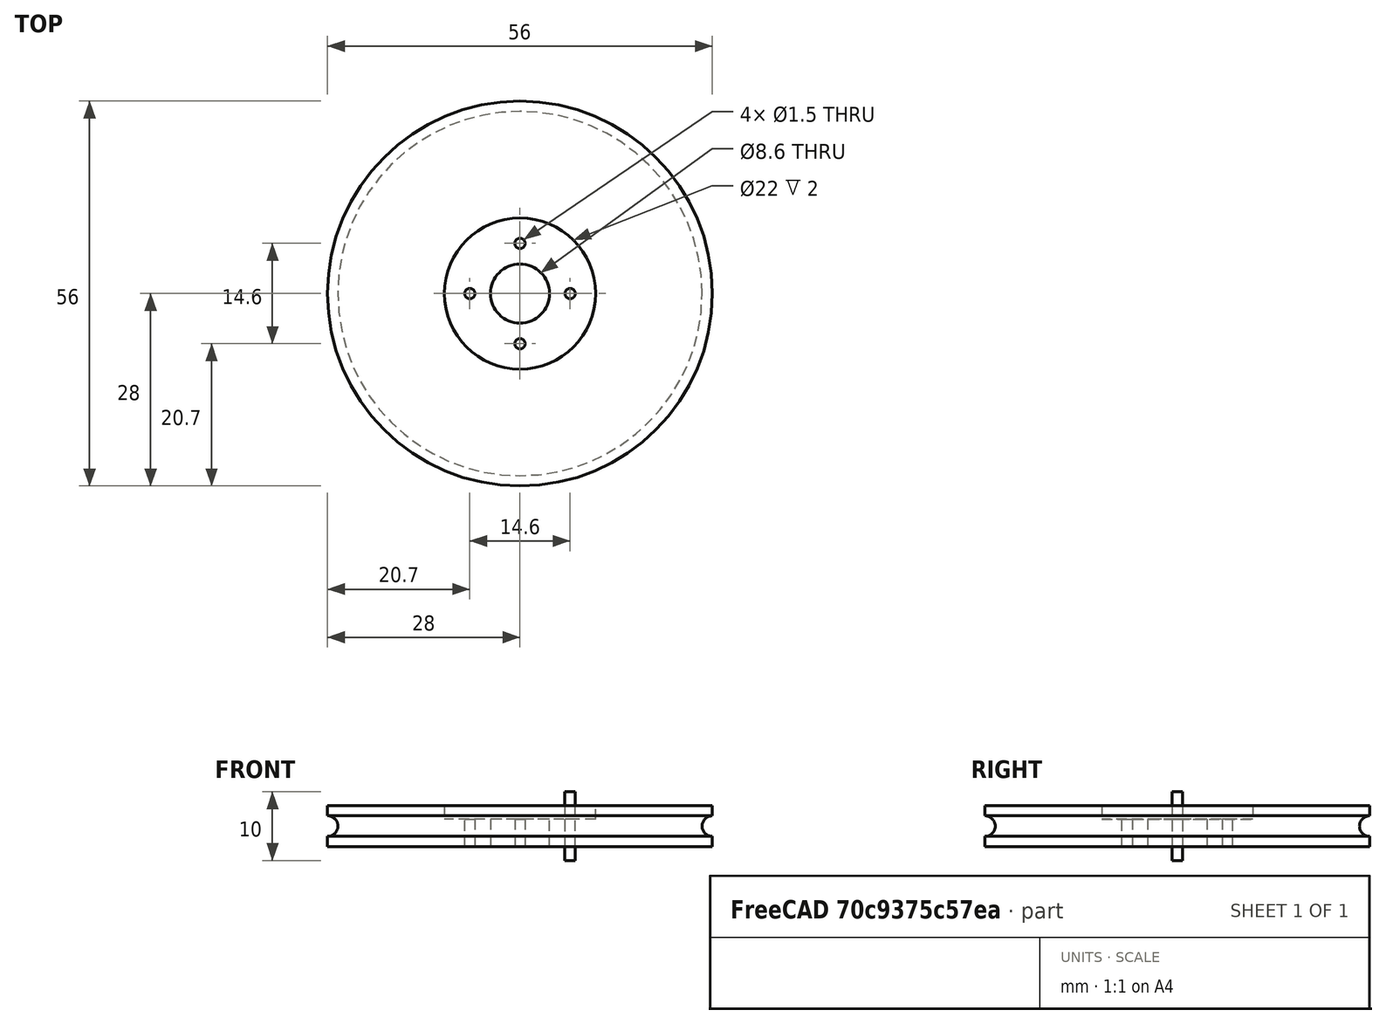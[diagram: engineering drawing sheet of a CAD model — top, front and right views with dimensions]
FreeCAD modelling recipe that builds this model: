
FCSTD DOCUMENT  (FreeCAD 0.20R29177 (Git))
Label: Video15
License: All rights reserved
LicenseURL: http://en.wikipedia.org/wiki/All_rights_reserved
objects: Part::Cylinder×4, Part::Cut×4, Part::Torus×1, Part::FeaturePython×1
note: 9 computed .brp shape members not serialized (recipe doc carries the construction recipe); baked Part::Feature solids carry a one-line shape summary decoded from their .brp

FEATURE [Part::Cylinder] Cylinder  label="Rueda base"
  Angle = 360
  AttacherType = Attacher::AttachEngine3D
  FirstAngle = 0
  Height = 6
  Placement = pos=(0,0,-3) rot=(0,0,1;0rad)
  Radius = 28
  SecondAngle = 0
FEATURE [Part::Torus] Torus  label="Hueco-Junta tórica"
  Angle1 = -180
  Angle2 = 180
  Angle3 = 360
  AttacherType = Attacher::AttachEngine3D
  Radius1 = 28
  Radius2 = 1.5
FEATURE [Part::Cut] Cut  label="Rueda basica"
  Base = -> Cylinder
  Tool = -> Torus
FEATURE [Part::Cylinder] Cylinder001  label="Corona servo"
  Angle = 360
  AttacherType = Attacher::AttachEngine3D
  FirstAngle = 0
  Height = 10
  Placement = pos=(0,0,1) rot=(0,0,1;0rad)
  Radius = 11
  SecondAngle = 0
FEATURE [Part::Cut] Cut001  label="Rueda con hueco corona"
  Base = -> Cut
  Tool = -> Cylinder001
FEATURE [Part::Cylinder] Cylinder002  label="Hueco del eje"
  Angle = 360
  AttacherType = Attacher::AttachEngine3D
  FirstAngle = 0
  Height = 10
  Placement = pos=(0,0,-4) rot=(0,0,1;0rad)
  Radius = 4.3
  SecondAngle = 0
FEATURE [Part::Cut] Cut002  label="Rueda corona eje"
  Base = -> Cut001
  Tool = -> Cylinder002
FEATURE [Part::Cylinder] Cylinder003  label="Taladro"
  Angle = 360
  AttacherType = Attacher::AttachEngine3D
  FirstAngle = 0
  Height = 10
  Placement = pos=(7.3,0,-5) rot=(0,0,1;0rad)
  Radius = 0.75
  SecondAngle = 0
FEATURE [Part::FeaturePython] Array  # Draft array (typed FeaturePython)
  AlwaysSyncPlacement = false
  Angle = 360
  ArrayType = 1
  Axis = (0,0,1)
  Base = -> Cylinder003
  Center = (0,0,0)
  Count = 4
  ExpandArray = false
  Fuse = false
  IntervalAxis = (0,0,0)
  IntervalX = (100,0,0)
  IntervalY = (0,100,0)
  IntervalZ = (0,0,100)
  NumberCircles = 3
  NumberPolar = 4
  NumberX = 2
  NumberY = 2
  NumberZ = 1
  PlacementList = 4 placements: [(7.3,0,-5),(1.77636e-15,7.3,-5),(-7.3,8.93992e-16,-5),(-1.77636e-15,-7.3,-5)]
  RadialDistance = 50
  ScaleList = (4) [(1,1,1),(1,1,1),(1,1,1),(1,1,1)]
  Symmetry = 1
  TangentialDistance = 25
FEATURE [Part::Cut] Cut003  label="Rueda MiniSkyBot"
  Base = -> Cut002
  Tool = -> Array
